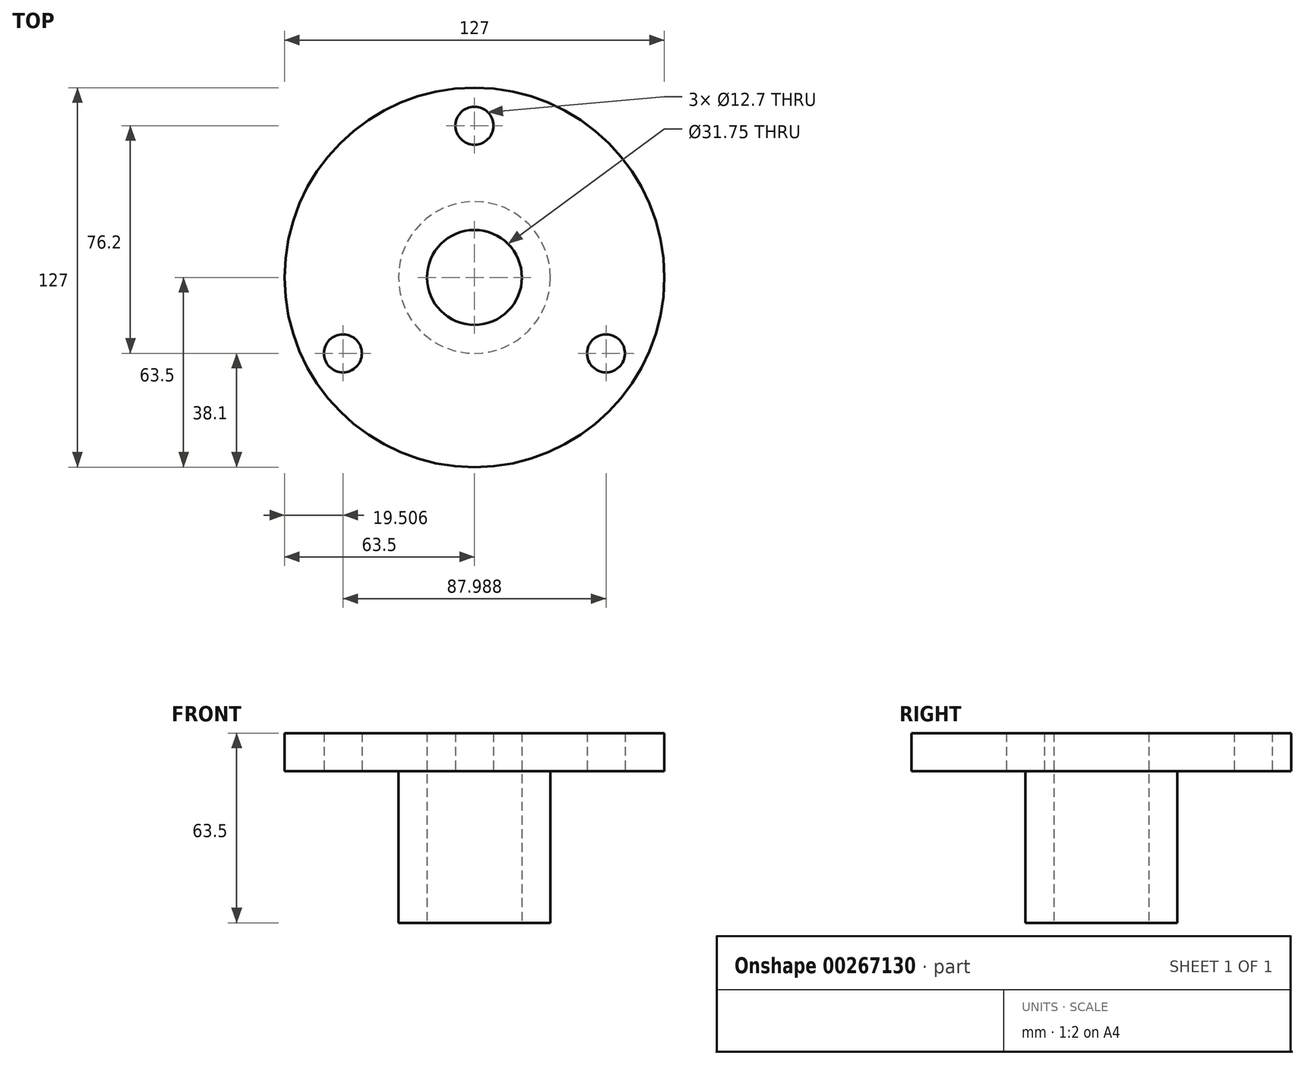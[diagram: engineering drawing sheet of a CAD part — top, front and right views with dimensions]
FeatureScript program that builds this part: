
annotation { "Feature Type Name" : "Feature", "Feature Type Description" : "" }
export const myFeature = defineFeature(function(context is Context, id is Id, definition is map)
    precondition{}
    {
        {
            var Q0;
            Q0=qCreatedBy(makeId("Top.planeOp"),FACE);
            var sketch = newSketch(context, id + "F0", { "sketchPlane" : qUnion([Q0])});
            skCircle(sketch, "E0", {"center": v(0, 0) * mm, "radius": 63.5 * mm});
            skCircle(sketch, "E1", {"center": v(0, 0) * mm, "radius": 25.4 * mm});
            skCircle(sketch, "E2", {"center": v(0, 50.8) * mm, "radius": 6.35 * mm});
            skCircle(sketch, "E3.1.0", {"center": v(-44, -25.4) * mm, "radius": 6.35 * mm});
            skCircle(sketch, "E3.2.0", {"center": v(44, -25.4) * mm, "radius": 6.35 * mm});
            skCircle(sketch, "E4", {"center": v(0, 0) * mm, "radius": 15.88 * mm});
            skSolve(sketch);
        }
        {
            var Q0;
            Q0=makeQuery(id+"F0.imprint","IMPRINT",FACE,{"disambiguationData":[TD([[makeQuery(id+"F0.imprint","IMPRINT",EDGE,{"derivedFrom":sQuery(id+"F0.wireOp",EDGE,"E0")}),1.0]])]});
            var Q1;
            Q1=makeQuery(id+"F0.imprint","IMPRINT",FACE,{"disambiguationData":[TD([[makeQuery(id+"F0.imprint","IMPRINT",EDGE,{"derivedFrom":sQuery(id+"F0.wireOp",EDGE,"E1")}),1.0]])]});
            extrude(context, id + "F1", {"entities" : qUnion([Q0, Q1]), "depth" : 12.7 * mm});
        }
        {
            var Q0;
            Q0=makeQuery(id+"F0.imprint","IMPRINT",FACE,{"disambiguationData":[TD([[makeQuery(id+"F0.imprint","IMPRINT",EDGE,{"derivedFrom":sQuery(id+"F0.wireOp",EDGE,"E1")}),1.0]])]});
            extrude(context, id + "F2", {"entities" : qUnion([Q0]), "operationType" : NewBodyOperationType.ADD, "oppositeDirection" : true, "depth" : 50.8 * mm});
        }
    });
